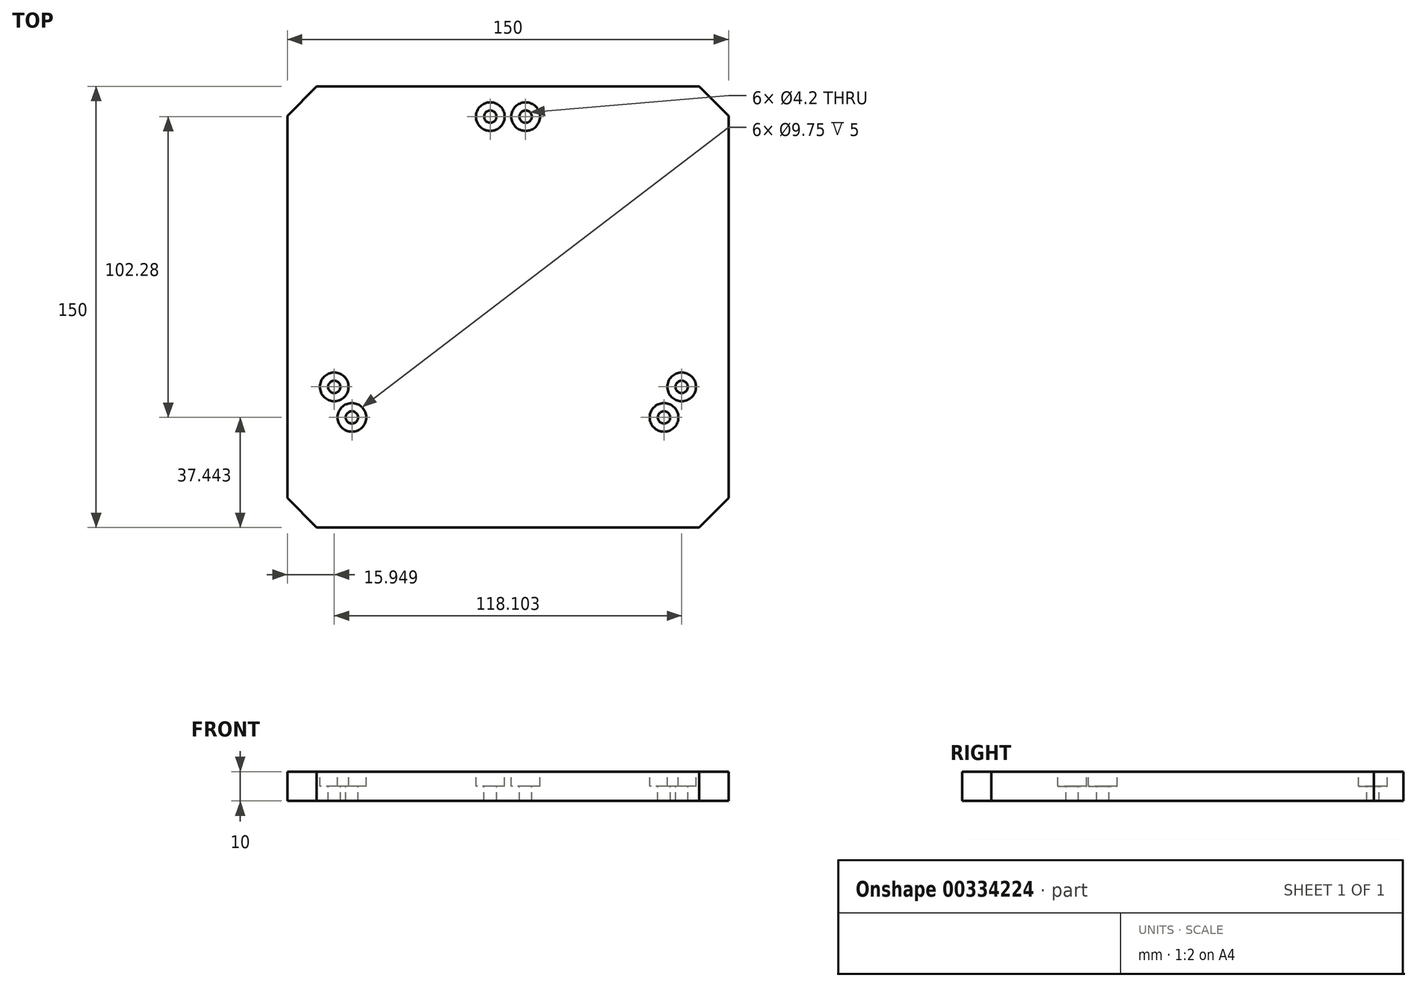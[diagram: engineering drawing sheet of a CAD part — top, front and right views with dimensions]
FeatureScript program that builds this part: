
annotation { "Feature Type Name" : "Feature", "Feature Type Description" : "" }
export const myFeature = defineFeature(function(context is Context, id is Id, definition is map)
    precondition{}
    {
        {
            var Q0;
            Q0=qCreatedBy(makeId("Top.planeOp"),FACE);
            var sketch = newSketch(context, id + "F0", { "sketchPlane" : qUnion([Q0])});
            skLineSegment(sketch, "E0", {"start": v(0, 219.4) * mm, "end": v(0, -234.81) * mm, "construction": true});
            skLineSegment(sketch, "E1", {"start": v(215.89, 0) * mm, "end": v(-218.7, 0) * mm, "construction": true});
            skLineSegment(sketch, "E2.bottom", {"start": v(-75, 75) * mm, "end": v(75, 75) * mm});
            skLineSegment(sketch, "E2.top", {"start": v(-75, -75) * mm, "end": v(75, -75) * mm});
            skLineSegment(sketch, "E2.left", {"start": v(-75, 75) * mm, "end": v(-75, -75) * mm});
            skLineSegment(sketch, "E2.right", {"start": v(75, 75) * mm, "end": v(75, -75) * mm});
            skSolve(sketch);
        }
        {
            var Q0;
            Q0 = qSketchRegion(id + "F0", true);
            extrude(context, id + "F1", {"entities" : qUnion([Q0]), "depth" : 10 * mm});
        }
        {
            var Q0;
            Q0=makeQuery(id+"F1.opExtrude","CAP_FACE",FACE,{"disambiguationData":[OSD([sQuery(id+"F0.wireOp",EDGE,"E2.bottom"),sQuery(id+"F0.wireOp",EDGE,"E2.top"),sQuery(id+"F0.wireOp",EDGE,"E2.left"),sQuery(id+"F0.wireOp",EDGE,"E2.right")])],"isStart":false});
            var sketch = newSketch(context, id + "F2", { "sketchPlane" : qUnion([Q0])});
            skLineSegment(sketch, "E3", {"start": v(0, 75) * mm, "end": v(0, -88.91) * mm, "construction": true});
            skLineSegment(sketch, "E4", {"start": v(75, 0) * mm, "end": v(-101.62, 0) * mm, "construction": true});
            skPoint(sketch, "E4.endSnap0", {"position": v(75, 0) * mm});
            skCircle(sketch, "E5", {"center": v(0, 0) * mm, "radius": 65 * mm, "construction": true});
            skPoint(sketch, "E6", {"position": v(-6, 64.72) * mm});
            skPoint(sketch, "E7", {"position": v(6, 64.72) * mm});
            skLineSegment(sketch, "E8", {"start": v(0, 0) * mm, "end": v(-70.4, -40.64) * mm, "construction": true});
            skLineSegment(sketch, "E9", {"start": v(0, 0) * mm, "end": v(107.14, -61.86) * mm, "construction": true});
            skPoint(sketch, "E10", {"position": v(-59.05, -27.17) * mm});
            skPoint(sketch, "E11", {"position": v(-53.05, -37.56) * mm});
            skPoint(sketch, "E12", {"position": v(53.05, -37.56) * mm});
            skPoint(sketch, "E13", {"position": v(59.05, -27.17) * mm});
            skSolve(sketch);
        }
        {
            var Q0;
            Q0=sQuery(id+"F2.wireOp",VERTEX,"E6");
            var Q1;
            Q1=sQuery(id+"F2.wireOp",VERTEX,"E7");
            var Q2;
            Q2=sQuery(id+"F2.wireOp",VERTEX,"E10");
            var Q3;
            Q3=sQuery(id+"F2.wireOp",VERTEX,"E11");
            var Q4;
            Q4=sQuery(id+"F2.wireOp",VERTEX,"E12");
            var Q5;
            Q5=sQuery(id+"F2.wireOp",VERTEX,"E13");
            var Q6;
            Q6=makeQuery(id+"F1.opExtrude","SWEPT_BODY",BODY,{"disambiguationData":[OSD([sQuery(id+"F0.wireOp",EDGE,"E2.bottom"),sQuery(id+"F0.wireOp",EDGE,"E2.top"),sQuery(id+"F0.wireOp",EDGE,"E2.left"),sQuery(id+"F0.wireOp",EDGE,"E2.right")])]});
            hole(context, id + "F3", {"style" : HoleStyle.C_BORE, "endStyle" : HoleEndStyle.BLIND, "standardTappedOrClearance" : lookupTablePath({ "standard" : "ISO", "engagement" : "75%", "pitch" : "0.8 mm", "size" : "M5", "type" : "Tapped" }), "standardBlindInLast" : lookupTablePath({ "standard" : "ISO", "engagement" : "75%", "pitch" : "0.8 mm", "size" : "M5", "type" : "Tapped" }), "holeDiameter" : 4.2 * mm, "cBoreDiameter" : 9.75 * mm, "cBoreDepth" : 5 * mm, "showTappedDepth" : true, "holeDepth" : 15.8 * mm, "tappedDepth" : 15 * mm, "tapClearance" : 1, "locations" : qUnion([Q0, Q1, Q2, Q3, Q4, Q5]), "scope" : qUnion([Q6]), "majorDiameter" : 5 * mm});
        }
        {
            var Q0;
            Q0=makeQuery(id+"F1.opExtrude","SWEPT_EDGE",EDGE,{"disambiguationData":[OSD([sQuery(id+"F0.wireOp",EDGE,"E2.bottom"),sQuery(id+"F0.wireOp",EDGE,"E2.left")])]});
            var Q1;
            Q1=makeQuery(id+"F1.opExtrude","SWEPT_EDGE",EDGE,{"disambiguationData":[OSD([sQuery(id+"F0.wireOp",EDGE,"E2.bottom"),sQuery(id+"F0.wireOp",EDGE,"E2.right")])]});
            var Q2;
            Q2=makeQuery(id+"F1.opExtrude","SWEPT_EDGE",EDGE,{"disambiguationData":[OSD([sQuery(id+"F0.wireOp",EDGE,"E2.top"),sQuery(id+"F0.wireOp",EDGE,"E2.right")])]});
            var Q3;
            Q3=makeQuery(id+"F1.opExtrude","SWEPT_EDGE",EDGE,{"disambiguationData":[OSD([sQuery(id+"F0.wireOp",EDGE,"E2.top"),sQuery(id+"F0.wireOp",EDGE,"E2.left")])]});
            chamfer(context, id + "F4", {"entities" : qUnion([Q0, Q1, Q2, Q3]), "width" : 10 * mm, "tangentPropagation" : true});
        }
    });
